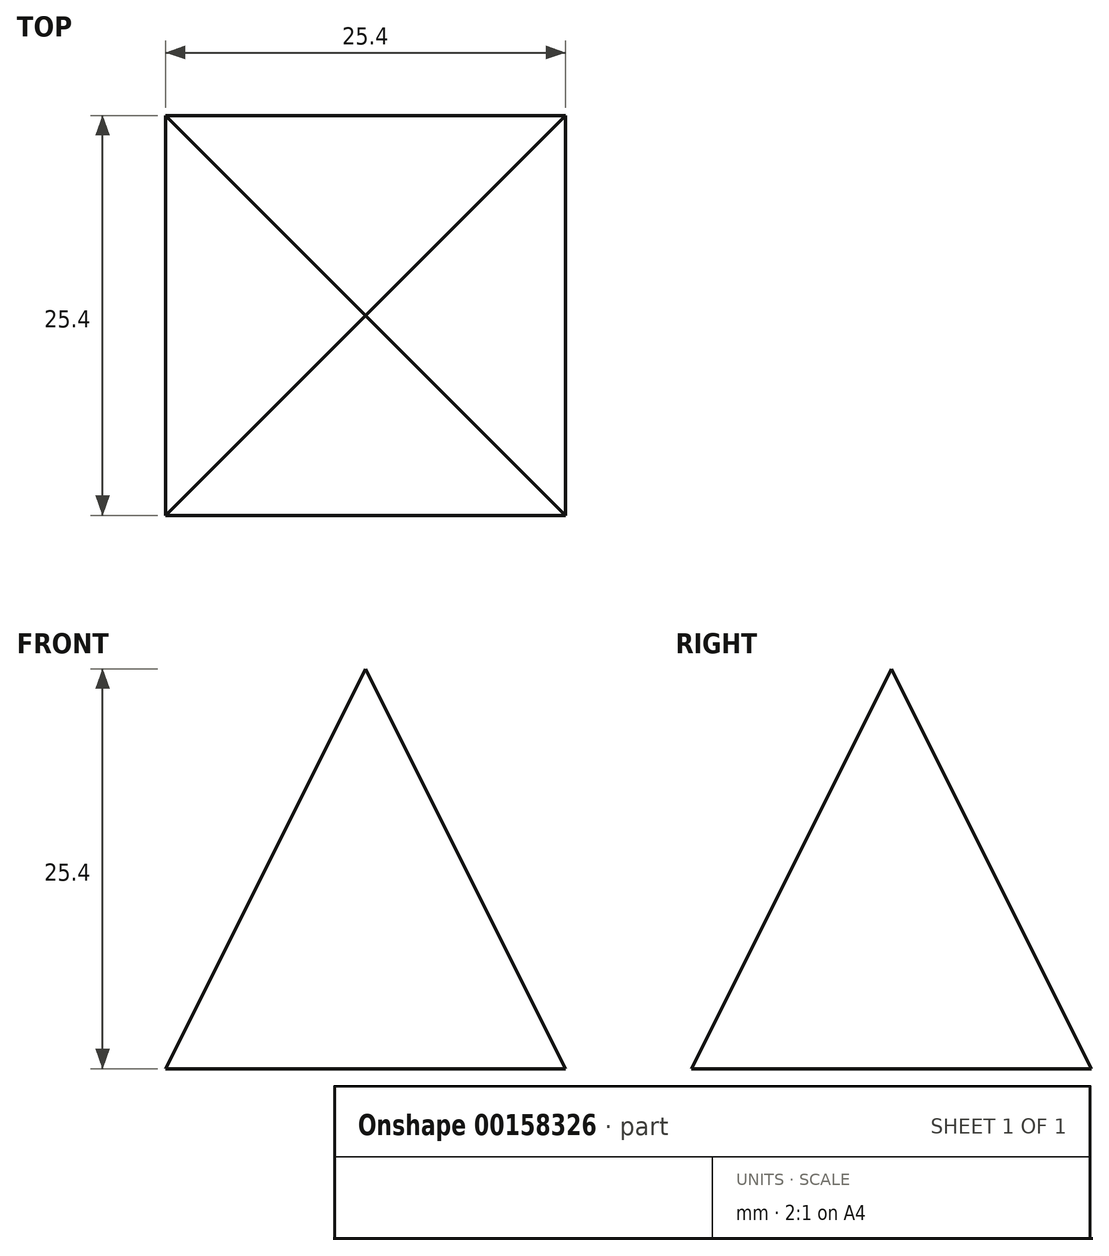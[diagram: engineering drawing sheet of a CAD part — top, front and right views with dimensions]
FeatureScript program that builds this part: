
annotation { "Feature Type Name" : "Feature", "Feature Type Description" : "" }
export const myFeature = defineFeature(function(context is Context, id is Id, definition is map)
    precondition{}
    {
        {
            assignVariable(context, id + "F0", {"name" : "height", "anyValue" : 25.4 * mm});
        }
        {
            var Q0;
            Q0=qCreatedBy(makeId("Top.planeOp"),FACE);
            var sketch = newSketch(context, id + "F1", { "sketchPlane" : qUnion([Q0])});
            skLineSegment(sketch, "E0.bottom", {"start": v(12.7, 12.7) * mm, "end": v(-12.7, 12.7) * mm});
            skLineSegment(sketch, "E0.top", {"start": v(12.7, -12.7) * mm, "end": v(-12.7, -12.7) * mm});
            skLineSegment(sketch, "E0.left", {"start": v(12.7, 12.7) * mm, "end": v(12.7, -12.7) * mm});
            skLineSegment(sketch, "E0.right", {"start": v(-12.7, 12.7) * mm, "end": v(-12.7, -12.7) * mm});
            skPoint(sketch, "E0.middle", {"position": v(0, 0) * mm});
            skSolve(sketch);
        }
        {
            var Q0;
            Q0=makeQuery(id+"F1.imprint","IMPRINT",FACE,{"disambiguationData":[TD([[makeQuery(id+"F1.imprint","IMPRINT",EDGE,{"derivedFrom":sQuery(id+"F1.wireOp",EDGE,"E0.bottom")}),1.0]])]});
            extrude(context, id + "F2", {"entities" : qUnion([Q0]), "depth" : getVariable(context, 'height')});
        }
        {
            var Q0;
            Q0=makeQuery(id+"F2.opExtrude","SWEPT_FACE",FACE,{"disambiguationData":[OSD([sQuery(id+"F1.wireOp",EDGE,"E0.top")])]});
            var sketch = newSketch(context, id + "F3", { "sketchPlane" : qUnion([Q0])});
            skLineSegment(sketch, "E1", {"start": v(-12.7, 0) * mm, "end": v(0, 25.4) * mm});
            skLineSegment(sketch, "E2", {"start": v(0, 25.4) * mm, "end": v(12.7, 0) * mm});
            skLineSegment(sketch, "E3", {"start": v(12.7, 0) * mm, "end": v(12.7, 25.4) * mm});
            skLineSegment(sketch, "E4", {"start": v(12.7, 25.4) * mm, "end": v(-12.7, 25.4) * mm});
            skLineSegment(sketch, "E5", {"start": v(-12.7, 25.4) * mm, "end": v(-12.7, 0) * mm});
            skSolve(sketch);
        }
        {
            var Q0;
            Q0=makeQuery(id+"F2.opExtrude","SWEPT_FACE",FACE,{"disambiguationData":[OSD([sQuery(id+"F1.wireOp",EDGE,"E0.left")])]});
            var sketch = newSketch(context, id + "F4", { "sketchPlane" : qUnion([Q0])});
            skLineSegment(sketch, "E6", {"start": v(-12.7, 0) * mm, "end": v(0, 25.4) * mm});
            skLineSegment(sketch, "E7", {"start": v(12.7, 0) * mm, "end": v(0, 25.4) * mm});
            skLineSegment(sketch, "E8", {"start": v(12.7, 0) * mm, "end": v(12.7, 25.4) * mm});
            skLineSegment(sketch, "E9", {"start": v(12.7, 25.4) * mm, "end": v(-12.7, 25.4) * mm});
            skLineSegment(sketch, "E10", {"start": v(-12.7, 25.4) * mm, "end": v(-12.7, 0) * mm});
            skSolve(sketch);
        }
        {
            var Q0;
            {var subQ0=sQuery(id+"F3.wireOp",EDGE,"E1");Q0=makeQuery(id+"F3.imprint","IMPRINT",FACE,{"disambiguationData":[TD([[makeQuery(id+"F3.imprint","IMPRINT",EDGE,{"derivedFrom":subQ0}),1.0]])]});}
            var Q1;
            {var subQ0=sQuery(id+"F3.wireOp",EDGE,"E2");Q1=makeQuery(id+"F3.imprint","IMPRINT",FACE,{"disambiguationData":[TD([[makeQuery(id+"F3.imprint","IMPRINT",EDGE,{"derivedFrom":subQ0}),1.0]])]});}
            extrude(context, id + "F5", {"entities" : qUnion([Q0, Q1]), "operationType" : NewBodyOperationType.REMOVE, "oppositeDirection" : true, "depth" : getVariable(context, 'height')});
        }
        {
            var Q0;
            {var subQ0=sQuery(id+"F4.wireOp",EDGE,"E6");Q0=makeQuery(id+"F4.imprint","IMPRINT",FACE,{"disambiguationData":[TD([[makeQuery(id+"F4.imprint","IMPRINT",EDGE,{"derivedFrom":subQ0}),1.0]])]});}
            var Q1;
            {var subQ0=sQuery(id+"F4.wireOp",EDGE,"E7");Q1=makeQuery(id+"F4.imprint","IMPRINT",FACE,{"disambiguationData":[TD([[makeQuery(id+"F4.imprint","IMPRINT",EDGE,{"derivedFrom":subQ0}),-1.0]])]});}
            extrude(context, id + "F6", {"entities" : qUnion([Q0, Q1]), "operationType" : NewBodyOperationType.REMOVE, "oppositeDirection" : true, "depth" : getVariable(context, 'height')});
        }
    });
